# Revit family: Lüftungsrohrschelle ,ohne AG, Gummi
name_source: partatom
category: HLS-Bauteile
revit_build: Autodesk Revit 2017 (Build: 20190507_1515(x64)
units: mm (PartAtom-declared; Revit-internal decimal feet)

## family parameters
Arbeitsebenenbasiert = Ja
Beim Laden mit Abzugskörper schneiden = Nein
Bemaßung runder Anschluss = Durchmesser verwenden
Gemeinsam genutzt = Ja
Immer vertikal = Nein
Raumberechnungspunkt = Nein
Teiletyp = Normal

## types (18) — shared parameters
Anschluss = ohne Anschluss
Bauart = zweiteilig
Baustoffklasse = B2
DF1 = 25 mm  [stored 0.082021 ft]
DS = 6 mm  [stored 0.019685 ft]
Dämmstärke = 6 mm  [stored 0.019685 ft]
Fabrikat = MEFA
Farbe Schalldämmeinlage = schwarz
Firma = MEFA Befestigungs- und Montagesysteme GmbH
MD = 3 mm  [stored 0.00984252 ft]
Material = Stahl
Material Schalldämmeinlage = TPE
Materialname = S235
Mengeneinheit = St
Oberflaeche = feuerbandverzinkt
Rohraußendurchmesser Zoll = Zoll
Schalldämmeinlage = Gummi
Verschluss = Mutter / Verschluss-Schraube
Vorgabe-Ansicht = 1219 mm
max. Temperaturbeständigkeit = 100 °C
max. zul. Last horizontal = 0.00 kN
max. zul. Last vertikal = 0.00 kN
vpe = 1 St
zero-valued in all types: A, HGA, Stärke Material, max. Rohraußendurchmesser, min. Rohraußendurchmesser

## per-type parameters (varying)
- Lüftungsrohrschelle, o.AG, o.VS, DN 224, Gummi: AB=1 mm  [stored 0.00328084 ft]; Achsabstand=274 mm; Artikelnummer=0432240; B=299 mm; Breite=299 mm; D=227 mm  [stored 0.744751 ft]; D0=239 mm  [stored 0.784121 ft]; DF2=34 mm; DVS=8 mm  [stored 0.0262467 ft]; EAN=4250928409904; Gewicht=0.44 kg; Gewicht pro Bauteil=0.44 kg; H=245 mm  [stored 0.803806 ft]; Höhe=245 mm; Kurztext1=Lüftungsschelle Standard 20x2,5; Kurztext2=DN 224 ohne Anschluss TPE; MB=20 mm  [stored 0.0656168 ft]; Materialmaße=20x2,5 mm; Nennweite DN Rohr=224 mm  [stored 0.734908 ft]; R=120 mm; RM=122 mm; Rohraußendurchmesser=227 mm  [stored 0.744751 ft]; S=274 mm; max. Höhe=245 mm  [stored 0.803806 ft]; max. zul. Last=1.50 kN
- Lüftungsrohrschelle, o.AG, o.VS, DN 250, Gummi: AB=1 mm  [stored 0.00328084 ft]; Achsabstand=300 mm; Artikelnummer=0432500; B=325 mm; Breite=325 mm; D=253 mm  [stored 0.830052 ft]; D0=265 mm; DF2=34 mm; DVS=8 mm  [stored 0.0262467 ft]; EAN=4250928409966; Gewicht=0.48 kg; Gewicht pro Bauteil=0.48 kg; H=271 mm; Höhe=271 mm; Kurztext1=Lüftungsschelle Standard 20x2,5; Kurztext2=DN 250 ohne Anschluss TPE; MB=20 mm  [stored 0.0656168 ft]; Materialmaße=20x2,5 mm; Nennweite DN Rohr=250 mm  [stored 0.82021 ft]; R=133 mm; RM=135 mm  [stored 0.442913 ft]; Rohraußendurchmesser=253 mm  [stored 0.830052 ft]; S=300 mm; max. Höhe=271 mm; max. zul. Last=1.50 kN
- Lüftungsrohrschelle, o.AG, o.VS, DN 280, Gummi: AB=3 mm  [stored 0.00984252 ft]; Achsabstand=331 mm; Artikelnummer=0432800; B=356 mm; Breite=356 mm; D=283 mm; D0=295 mm; DF2=35 mm  [stored 0.114829 ft]; DVS=8 mm  [stored 0.0262467 ft]; EAN=4250928410023; Gewicht=0.65 kg; Gewicht pro Bauteil=0.65 kg; H=303 mm; Höhe=303 mm; Kurztext1=Lüftungsschelle Standard 25x2,5; Kurztext2=DN 280 ohne Anschluss TPE; MB=25 mm  [stored 0.082021 ft]; Materialmaße=25x2,5 mm; Nennweite DN Rohr=280 mm; R=148 mm; RM=150 mm; Rohraußendurchmesser=283 mm; S=331 mm; max. Höhe=303 mm; max. zul. Last=2.00 kN
- Lüftungsrohrschelle, o.AG, o.VS, DN 300, Gummi: AB=4 mm  [stored 0.0131234 ft]; Achsabstand=353 mm; Artikelnummer=0433000; B=378 mm; Breite=378 mm; D=304 mm; D0=316 mm; DF2=36 mm  [stored 0.11811 ft]; DVS=8 mm  [stored 0.0262467 ft]; EAN=4250928410085; Gewicht=0.70 kg; Gewicht pro Bauteil=0.70 kg; H=325 mm; Höhe=325 mm; Kurztext1=Lüftungsschelle Standard 25x2,5; Kurztext2=DN 300 ohne Anschluss TPE; MB=25 mm  [stored 0.082021 ft]; Materialmaße=25x2,5 mm; Nennweite DN Rohr=300 mm; R=158 mm  [stored 0.518373 ft]; RM=161 mm; Rohraußendurchmesser=304 mm; S=353 mm; max. Höhe=325 mm; max. zul. Last=2.00 kN
- Lüftungsrohrschelle, o.AG, o.VS, DN 315, Gummi: AB=4 mm  [stored 0.0131234 ft]; Achsabstand=368 mm; Artikelnummer=0433150; B=393 mm; Breite=393 mm; D=319 mm; D0=331 mm; DF2=36 mm  [stored 0.11811 ft]; DVS=8 mm  [stored 0.0262467 ft]; EAN=4250928410146; Gewicht=0.73 kg; Gewicht pro Bauteil=0.73 kg; H=340 mm; Höhe=340 mm; Kurztext1=Lüftungsschelle Standard 25x2,5; Kurztext2=DN 315 ohne Anschluss TPE; MB=25 mm  [stored 0.082021 ft]; Materialmaße=25x2,5 mm; Nennweite DN Rohr=315 mm; R=166 mm; RM=168 mm  [stored 0.551181 ft]; Rohraußendurchmesser=319 mm; S=368 mm; max. Höhe=340 mm; max. zul. Last=2.00 kN
- Lüftungsrohrschelle, o.AG, o.VS, DN 355, Gummi: AB=4 mm  [stored 0.0131234 ft]; Achsabstand=408 mm; Artikelnummer=0433550; B=433 mm; Breite=433 mm; D=359 mm; D0=371 mm; DF2=36 mm  [stored 0.11811 ft]; DVS=8 mm  [stored 0.0262467 ft]; EAN=4250928410207; Gewicht=0.81 kg; Gewicht pro Bauteil=0.81 kg; H=380 mm; Höhe=380 mm; Kurztext1=Lüftungsschelle Standard 25x2,5; Kurztext2=DN 355 ohne Anschluss TPE; MB=25 mm  [stored 0.082021 ft]; Materialmaße=25x2,5 mm; Nennweite DN Rohr=355 mm; R=186 mm; RM=188 mm  [stored 0.616798 ft]; Rohraußendurchmesser=359 mm; S=408 mm; max. Höhe=380 mm; max. zul. Last=2.00 kN
- Lüftungsrohrschelle, o.AG, o.VS, DN 400, Gummi: AB=4 mm  [stored 0.0131234 ft]; Achsabstand=453 mm; Artikelnummer=0434000; B=478 mm; Breite=478 mm; D=404 mm; D0=416 mm; DF2=36 mm  [stored 0.11811 ft]; DVS=8 mm  [stored 0.0262467 ft]; EAN=4250928410269; Gewicht=0.90 kg; Gewicht pro Bauteil=0.90 kg; H=425 mm; Höhe=425 mm; Kurztext1=Lüftungsschelle Standard 25x2,5; Kurztext2=DN 400 ohne Anschluss TPE; MB=25 mm  [stored 0.082021 ft]; Materialmaße=25x2,5 mm; Nennweite DN Rohr=400 mm; R=208 mm  [stored 0.682415 ft]; RM=211 mm; Rohraußendurchmesser=404 mm; S=453 mm; max. Höhe=425 mm; max. zul. Last=2.00 kN
- Lüftungsrohrschelle, o.AG, o.VS, DN 450, Gummi: AB=4 mm  [stored 0.0131234 ft]; Achsabstand=503 mm; Artikelnummer=0434500; B=528 mm; Breite=528 mm; D=454 mm; D0=466 mm; DF2=36 mm  [stored 0.11811 ft]; DVS=8 mm  [stored 0.0262467 ft]; EAN=4250928410320; Gewicht=1.01 kg; Gewicht pro Bauteil=1.01 kg; H=475 mm; Höhe=475 mm; Kurztext1=Lüftungsschelle Standard 25x2,5; Kurztext2=DN 450 ohne Anschluss TPE; MB=25 mm  [stored 0.082021 ft]; Materialmaße=25x2,5 mm; Nennweite DN Rohr=450 mm; R=233 mm  [stored 0.764436 ft]; RM=236 mm; Rohraußendurchmesser=454 mm; S=503 mm; max. Höhe=475 mm; max. zul. Last=2.00 kN
- Lüftungsrohrschelle, o.AG, o.VS, DN 500, Gummi: AB=4 mm  [stored 0.0131234 ft]; Achsabstand=553 mm; Artikelnummer=0435000; B=578 mm; Breite=578 mm; D=504 mm; D0=516 mm; DF2=36 mm  [stored 0.11811 ft]; DVS=8 mm  [stored 0.0262467 ft]; EAN=4250928410382; Gewicht=1.11 kg; Gewicht pro Bauteil=1.11 kg; H=525 mm; Höhe=525 mm; Kurztext1=Lüftungsschelle Standard 25x2,5; Kurztext2=DN 500 ohne Anschluss TPE; MB=25 mm  [stored 0.082021 ft]; Materialmaße=25x2,5 mm; Nennweite DN Rohr=500 mm; R=258 mm  [stored 0.846457 ft]; RM=261 mm; Rohraußendurchmesser=504 mm; S=553 mm; max. Höhe=525 mm; max. zul. Last=2.00 kN
- Lüftungsrohrschelle, o.AG, o.VS, DN 560, Gummi: AB=4 mm  [stored 0.0131234 ft]; Achsabstand=613 mm; Artikelnummer=0435600; B=638 mm; Breite=638 mm; D=564 mm; D0=576 mm; DF2=36 mm  [stored 0.11811 ft]; DVS=8 mm  [stored 0.0262467 ft]; EAN=4250928410443; Gewicht=1.24 kg; Gewicht pro Bauteil=1.24 kg; H=585 mm; Höhe=585 mm; Kurztext1=Lüftungsschelle Standard 25x2,5; Kurztext2=DN 560 ohne Anschluss TPE; MB=25 mm  [stored 0.082021 ft]; Materialmaße=25x2,5 mm; Nennweite DN Rohr=560 mm; R=288 mm; RM=291 mm; Rohraußendurchmesser=564 mm; S=613 mm; max. Höhe=585 mm; max. zul. Last=2.00 kN
- Lüftungsrohrschelle, o.AG, o.VS, DN 600, Gummi: AB=4 mm  [stored 0.0131234 ft]; Achsabstand=651 mm; Artikelnummer=0436000; B=678 mm; Breite=676 mm; D=604 mm; D0=616 mm; DF2=36 mm  [stored 0.11811 ft]; DVS=8 mm  [stored 0.0262467 ft]; EAN=4250928410504; Gewicht=1.32 kg; Gewicht pro Bauteil=1.32 kg; H=625 mm; Höhe=621 mm; Kurztext1=Lüftungsschelle Standard 25x2,5; Kurztext2=DN 600 ohne Anschluss TPE; MB=25 mm  [stored 0.082021 ft]; Materialmaße=25x2,5 mm; Nennweite DN Rohr=600 mm; R=308 mm; RM=311 mm; Rohraußendurchmesser=605 mm; S=653 mm; max. Höhe=621 mm; max. zul. Last=2.00 kN
- Lüftungsrohrschelle, o.AG, o.VS, DN 630, Gummi: AB=4 mm  [stored 0.0131234 ft]; Achsabstand=651 mm; Artikelnummer=0436000; B=711 mm; Breite=676 mm; D=635 mm; D0=647 mm; DF2=35 mm  [stored 0.114829 ft]; DVS=10 mm  [stored 0.0328084 ft]; EAN=4250928410504; Gewicht=1.32 kg; Gewicht pro Bauteil=1.32 kg; H=657 mm; Höhe=621 mm; Kurztext1=Lüftungsschelle Standard 25x2,5; Kurztext2=DN 600 ohne Anschluss TPE; MB=25 mm  [stored 0.082021 ft]; Materialmaße=25x2,5 mm; Nennweite DN Rohr=600 mm; R=324 mm; RM=327 mm; Rohraußendurchmesser=605 mm; S=686 mm; max. Höhe=621 mm; max. zul. Last=2.00 kN
- Lüftungsrohrschelle, o.AG, o.VS, DN 710, Gummi: AB=4 mm  [stored 0.0131234 ft]; Achsabstand=766 mm; Artikelnummer=0437100; B=791 mm; Breite=791 mm; D=715 mm; D0=727 mm; DF2=35 mm  [stored 0.114829 ft]; DVS=10 mm  [stored 0.0328084 ft]; EAN=4250928410542; Gewicht=1.79 kg; Gewicht pro Bauteil=1.79 kg; H=737 mm; Höhe=737 mm; Kurztext1=Lüftungsschelle Standard 25x3,0; Kurztext2=DN 710 ohne Anschluss TPE; MB=25 mm  [stored 0.082021 ft]; Materialmaße=25x3,0 mm; Nennweite DN Rohr=710 mm; R=364 mm; RM=367 mm; Rohraußendurchmesser=715 mm; S=766 mm; max. Höhe=737 mm; max. zul. Last=2.00 kN
- Lüftungsrohrschelle, o.AG, o.VS, DN 800, Gummi: AB=5 mm  [stored 0.0164042 ft]; Achsabstand=857 mm; Artikelnummer=0438000; B=882 mm; Breite=882 mm; D=805 mm; D0=817 mm; DF2=36 mm  [stored 0.11811 ft]; DVS=10 mm  [stored 0.0328084 ft]; EAN=4250928410566; Gewicht=2.01 kg; Gewicht pro Bauteil=2.01 kg; H=828 mm; Höhe=828 mm; Kurztext1=Lüftungsschelle Standard 25x3,0; Kurztext2=DN 800 ohne Anschluss TPE; MB=25 mm  [stored 0.082021 ft]; Materialmaße=25x3,0 mm; Nennweite DN Rohr=800 mm; R=409 mm; RM=412 mm; Rohraußendurchmesser=805 mm; S=857 mm; max. Höhe=828 mm; max. zul. Last=2.00 kN
- Lüftungsrohrschelle, o.AG, o.VS, DN 900, Gummi: AB=5 mm  [stored 0.0164042 ft]; Achsabstand=957 mm; Artikelnummer=0439000; B=982 mm; Breite=982 mm; D=905 mm; D0=917 mm; DF2=36 mm  [stored 0.11811 ft]; DVS=10 mm  [stored 0.0328084 ft]; EAN=4250928410580; Gewicht=2.75 kg; Gewicht pro Bauteil=2.75 kg; H=928 mm; Höhe=928 mm; Kurztext1=Lüftungsschelle Standard 30x3,0; Kurztext2=DN 900 ohne Anschluss TPE; MB=30 mm  [stored 0.0984252 ft]; Materialmaße=30x3,0 mm; Nennweite DN Rohr=900 mm; R=459 mm; RM=462 mm; Rohraußendurchmesser=905 mm; S=957 mm; max. Höhe=928 mm; max. zul. Last=2.00 kN
- Lüftungsrohrschelle, o.AG, o.VS, DN1000, Gummi: AB=6 mm  [stored 0.019685 ft]; Achsabstand=1059 mm; Artikelnummer=0440000; B=1084 mm; Breite=1 mm  [stored 0.00328084 ft]; D=1006 mm; D0=1018 mm; DF2=37 mm  [stored 0.121391 ft]; DVS=10 mm  [stored 0.0328084 ft]; EAN=4250928410603; Gewicht=3.04 kg; Gewicht pro Bauteil=3.04 kg; H=1030 mm; Höhe=1030 mm; Kurztext1=Lüftungsschelle Standard 30x3,0; Kurztext2=DN 1000 ohne Anschluss TPE; MB=30 mm  [stored 0.0984252 ft]; Materialmaße=30x3,0 mm; Nennweite DN Rohr=1 mm  [stored 0.00328084 ft]; R=509 mm; RM=512 mm; Rohraußendurchmesser=1006 mm; S=1059 mm; max. Höhe=1 mm  [stored 0.00328084 ft]; max. zul. Last=2.00 kN
- Lüftungsrohrschelle, o.AG, o.VS, DN1120, Gummi: AB=6 mm  [stored 0.019685 ft]; Achsabstand=1179 mm; Artikelnummer=0441200; B=1204 mm; Breite=1 mm  [stored 0.00328084 ft]; D=1126 mm; D0=1138 mm; DF2=37 mm  [stored 0.121391 ft]; DVS=10 mm  [stored 0.0328084 ft]; EAN=4250928410627; Gewicht=3.39 kg; Gewicht pro Bauteil=3.39 kg; H=1150 mm; Höhe=1150 mm; Kurztext1=Lüftungsschelle Standard 30x3,0; Kurztext2=DN 1120 ohne Anschluss TPE; MB=30 mm  [stored 0.0984252 ft]; Materialmaße=30x3,0 mm; Nennweite DN Rohr=1 mm  [stored 0.00328084 ft]; R=569 mm; RM=572 mm; Rohraußendurchmesser=1126 mm; S=1179 mm; max. Höhe=1 mm  [stored 0.00328084 ft]; max. zul. Last=2.00 kN
- Lüftungsrohrschelle, o.AG, o.VS, DN1250, Gummi: AB=6 mm  [stored 0.019685 ft]; Achsabstand=1309 mm; Artikelnummer=0442500; B=1334 mm; Breite=1 mm  [stored 0.00328084 ft]; D=1256 mm; D0=1268 mm; DF2=37 mm  [stored 0.121391 ft]; DVS=10 mm  [stored 0.0328084 ft]; EAN=4250928410641; Gewicht=3.77 kg; Gewicht pro Bauteil=3.77 kg; H=1280 mm; Höhe=1280 mm; Kurztext1=Lüftungsschelle Standard 30x3,0; Kurztext2=DN 1250 ohne Anschluss TPE; MB=30 mm  [stored 0.0984252 ft]; Materialmaße=30x3,0 mm; Nennweite DN Rohr=1 mm  [stored 0.00328084 ft]; R=634 mm; RM=637 mm; Rohraußendurchmesser=1256 mm; S=1309 mm; max. Höhe=1 mm  [stored 0.00328084 ft]; max. zul. Last=2.00 kN

note: [stored X ft] marks values corroborated as IEEE doubles in the binary element streams (Revit-internal decimal feet)

## geometry (parser evidence)
native form markers: Sweep x8
no freeform markers — native parametric forms only
